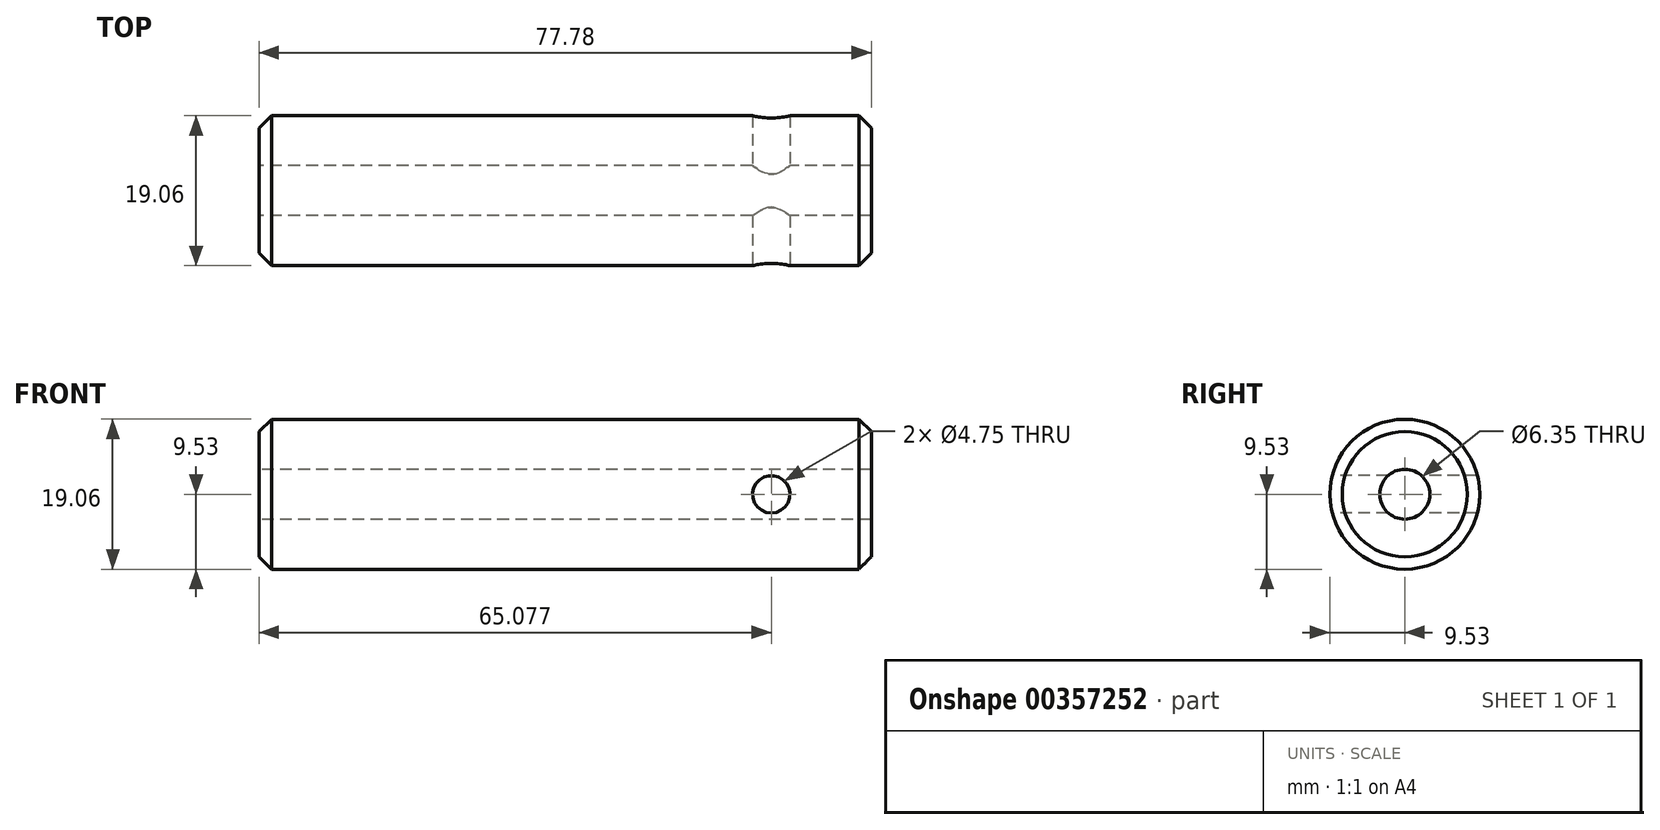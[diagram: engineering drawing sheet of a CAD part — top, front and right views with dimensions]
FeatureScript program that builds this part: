
annotation { "Feature Type Name" : "Feature", "Feature Type Description" : "" }
export const myFeature = defineFeature(function(context is Context, id is Id, definition is map)
    precondition{}
    {
        {
            var Q0;
            Q0=qCreatedBy(makeId("Right.planeOp"),FACE);
            var sketch = newSketch(context, id + "F0", { "sketchPlane" : qUnion([Q0])});
            skCircle(sketch, "E0", {"center": v(0, 0) * mm, "radius": 9.53 * mm});
            skCircle(sketch, "E1", {"center": v(0, 0) * mm, "radius": 3.18 * mm});
            skSolve(sketch);
        }
        {
            var Q0;
            Q0=makeQuery(id+"F0.imprint","IMPRINT",FACE,{"disambiguationData":[TD([[makeQuery(id+"F0.imprint","IMPRINT",EDGE,{"derivedFrom":sQuery(id+"F0.wireOp",EDGE,"E0")}),1.0]])]});
            extrude(context, id + "F1", {"entities" : qUnion([Q0]), "endBound" : BoundingType.SYMMETRIC, "depth" : 77.77 * mm});
        }
        {
            var Q0;
            Q0=makeQuery(id+"F1.opExtrude","CAP_EDGE",EDGE,{"disambiguationData":[OSD([sQuery(id+"F0.wireOp",EDGE,"E0")])],"isStart":false});
            chamfer(context, id + "F2", {"entities" : qUnion([Q0]), "chamferType" : ChamferType.OFFSET_ANGLE, "width" : 1.57 * mm, "oppositeDirection" : false, "angle" : 45 * degree, "tangentPropagation" : true});
        }
        {
            var Q0;
            Q0=makeQuery(id+"F1.opExtrude","CAP_EDGE",EDGE,{"disambiguationData":[OSD([sQuery(id+"F0.wireOp",EDGE,"E0")])],"isStart":true});
            chamfer(context, id + "F3", {"entities" : qUnion([Q0]), "chamferType" : ChamferType.OFFSET_ANGLE, "width" : 1.57 * mm, "oppositeDirection" : false, "angle" : 45 * degree, "tangentPropagation" : true});
        }
        {
            var Q0;
            Q0=qCreatedBy(makeId("Front.planeOp"),FACE);
            var sketch = newSketch(context, id + "F4", { "sketchPlane" : qUnion([Q0])});
            skCircle(sketch, "E2", {"center": v(26.19, 0) * mm, "radius": 2.37 * mm});
            skSolve(sketch);
        }
        {
            var Q0;
            Q0 = qSketchRegion(id + "F4", true);
            extrude(context, id + "F5", {"entities" : qUnion([Q0]), "operationType" : NewBodyOperationType.REMOVE, "endBound" : BoundingType.SYMMETRIC, "oppositeDirection" : true, "depth" : 25.4 * mm});
        }
    });
